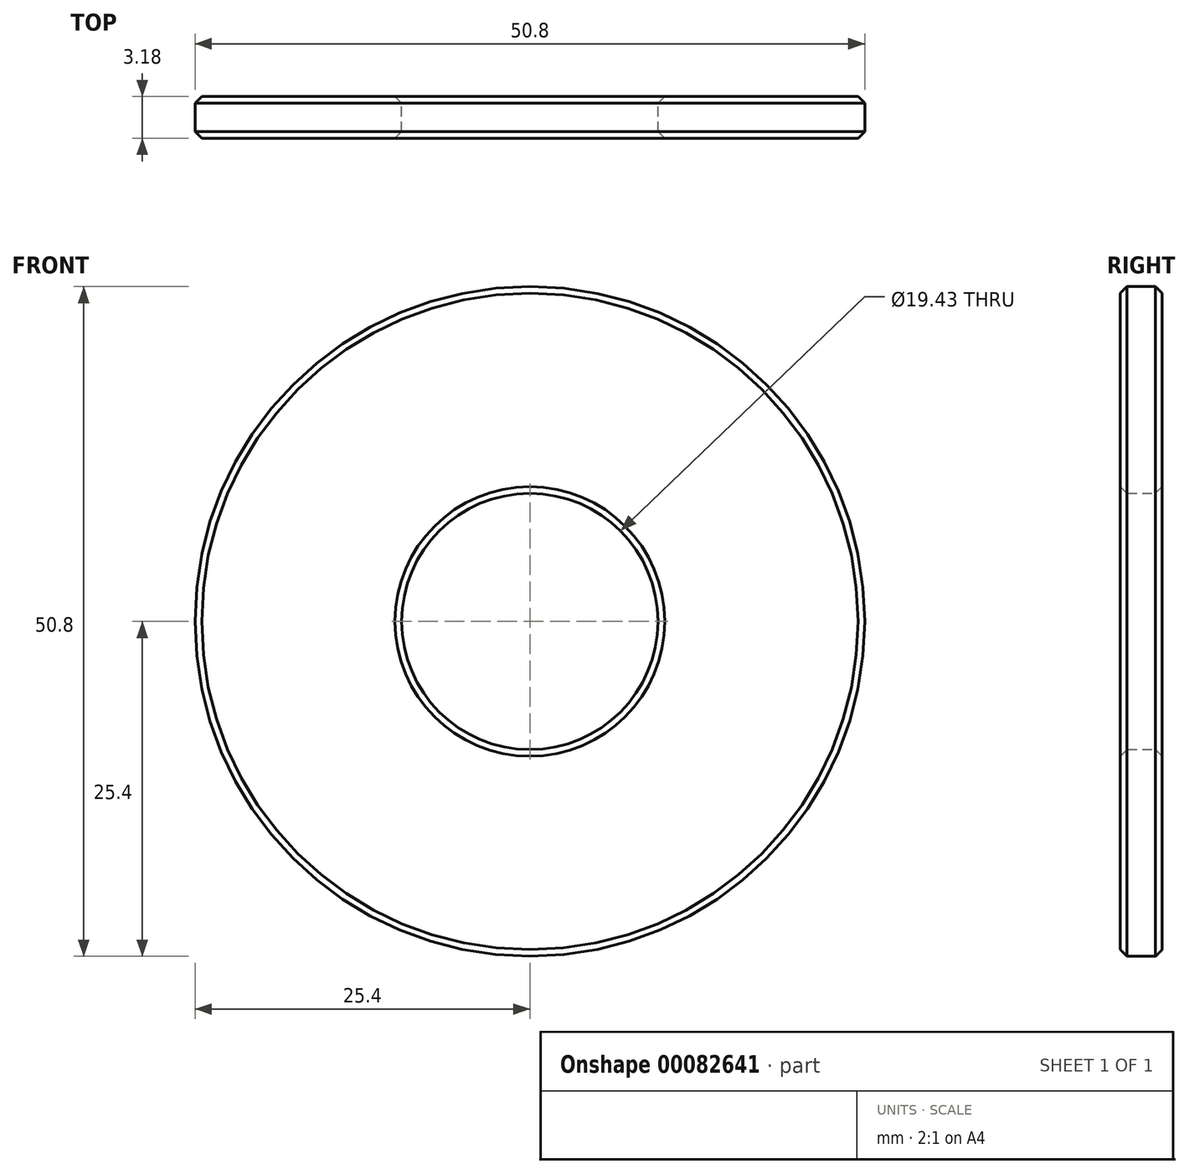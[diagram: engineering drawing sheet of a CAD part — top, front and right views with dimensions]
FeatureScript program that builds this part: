
annotation { "Feature Type Name" : "Feature", "Feature Type Description" : "" }
export const myFeature = defineFeature(function(context is Context, id is Id, definition is map)
    precondition{}
    {
        {
            var Q0;
            Q0=qCreatedBy(makeId("Front.planeOp"),FACE);
            var sketch = newSketch(context, id + "F0", { "sketchPlane" : qUnion([Q0])});
            skCircle(sketch, "E0", {"center": v(0, 0) * mm, "radius": 25.4 * mm});
            skCircle(sketch, "E1", {"center": v(0, 0) * mm, "radius": 9.72 * mm});
            skSolve(sketch);
        }
        {
            var Q0;
            Q0 = qSketchRegion(id + "F0", true);
            extrude(context, id + "F1", {"entities" : qUnion([Q0]), "depth" : 3.17 * mm});
        }
        {
            var Q0;
            Q0=makeQuery(id+"F1.opExtrude","CAP_EDGE",EDGE,{"disambiguationData":[OSD([sQuery(id+"F0.wireOp",EDGE,"E0")])],"isStart":false});
            var Q1;
            Q1=makeQuery(id+"F1.opExtrude","CAP_EDGE",EDGE,{"disambiguationData":[OSD([sQuery(id+"F0.wireOp",EDGE,"E0")])],"isStart":true});
            var Q2;
            Q2=makeQuery(id+"F1.opExtrude","CAP_EDGE",EDGE,{"disambiguationData":[OSD([sQuery(id+"F0.wireOp",EDGE,"E1")])],"isStart":false});
            var Q3;
            Q3=makeQuery(id+"F1.opExtrude","CAP_EDGE",EDGE,{"disambiguationData":[OSD([sQuery(id+"F0.wireOp",EDGE,"E1")])],"isStart":true});
            chamfer(context, id + "F2", {"entities" : qUnion([Q0, Q1, Q2, Q3]), "width" : 0.5 * mm, "tangentPropagation" : true});
        }
    });
